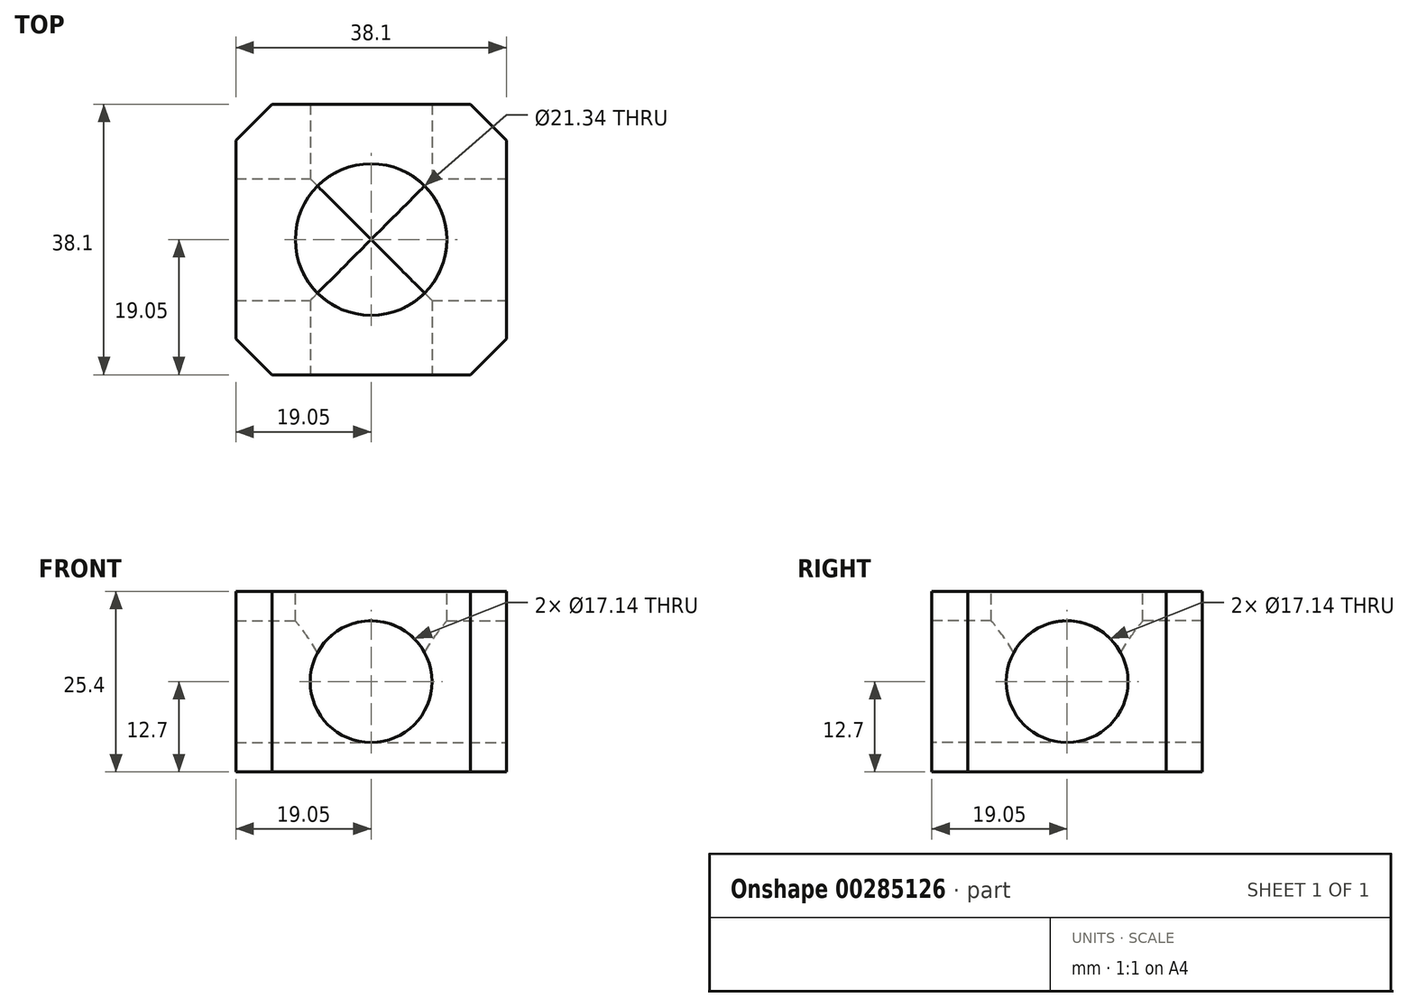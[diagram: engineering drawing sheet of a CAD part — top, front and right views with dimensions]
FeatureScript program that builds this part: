
annotation { "Feature Type Name" : "Feature", "Feature Type Description" : "" }
export const myFeature = defineFeature(function(context is Context, id is Id, definition is map)
    precondition{}
    {
        {
            var Q0;
            Q0=qCreatedBy(makeId("Top.planeOp"),FACE);
            var sketch = newSketch(context, id + "F0", { "sketchPlane" : qUnion([Q0])});
            skLineSegment(sketch, "E0.bottom", {"start": v(19.05, -19.05) * mm, "end": v(-19.05, -19.05) * mm});
            skLineSegment(sketch, "E0.top", {"start": v(19.05, 19.05) * mm, "end": v(-19.05, 19.05) * mm});
            skLineSegment(sketch, "E0.left", {"start": v(19.05, -19.05) * mm, "end": v(19.05, 19.05) * mm});
            skLineSegment(sketch, "E0.right", {"start": v(-19.05, -19.05) * mm, "end": v(-19.05, 19.05) * mm});
            skPoint(sketch, "E0.middle", {"position": v(0, 0) * mm});
            skSolve(sketch);
        }
        {
            var Q0;
            Q0=qSketchRegion(id+"F0",true);
            extrude(context, id + "F1", {"entities" : qUnion([Q0]), "depth" : 25.4 * mm});
        }
        {
            var Q0;
            Q0=makeQuery(id+"F1.opExtrude","CAP_FACE",FACE,{"disambiguationData":[OSD([sQuery(id+"F0.wireOp",EDGE,"E0.bottom"),sQuery(id+"F0.wireOp",EDGE,"E0.top"),sQuery(id+"F0.wireOp",EDGE,"E0.left"),sQuery(id+"F0.wireOp",EDGE,"E0.right")])],"isStart":false});
            var sketch = newSketch(context, id + "F2", { "sketchPlane" : qUnion([Q0])});
            skCircle(sketch, "E1", {"center": v(0, 0) * mm, "radius": 10.67 * mm});
            skSolve(sketch);
        }
        {
            var Q0;
            Q0=makeQuery(id+"F1.opExtrude","SWEPT_FACE",FACE,{"disambiguationData":[OSD([sQuery(id+"F0.wireOp",EDGE,"E0.bottom")])]});
            var sketch = newSketch(context, id + "F3", { "sketchPlane" : qUnion([Q0])});
            skLineSegment(sketch, "E2", {"start": v(0, 0) * mm, "end": v(0, 25.4) * mm});
            skLineSegment(sketch, "E3", {"start": v(0, 25.4) * mm, "end": v(0, 12.7) * mm});
            skCircle(sketch, "E4", {"center": v(0, 12.7) * mm, "radius": 8.57 * mm});
            skSolve(sketch);
        }
        {
            var Q0;
            Q0=qSketchRegion(id+"F3",true);
            extrude(context, id + "F4", {"entities" : qUnion([Q0]), "operationType" : NewBodyOperationType.REMOVE, "oppositeDirection" : true, "depth" : 76.2 * mm});
        }
        {
            var Q0;
            Q0=makeQuery(id+"F1.opExtrude","SWEPT_FACE",FACE,{"disambiguationData":[OSD([sQuery(id+"F0.wireOp",EDGE,"E0.left")])]});
            var sketch = newSketch(context, id + "F5", { "sketchPlane" : qUnion([Q0])});
            skLineSegment(sketch, "E5", {"start": v(0, 0) * mm, "end": v(0, 25.4) * mm});
            skLineSegment(sketch, "E6", {"start": v(0, 25.4) * mm, "end": v(0, 12.7) * mm});
            skCircle(sketch, "E7", {"center": v(0, 12.7) * mm, "radius": 8.57 * mm});
            skSolve(sketch);
        }
        {
            var Q0;
            Q0=qSketchRegion(id+"F5",true);
            extrude(context, id + "F6", {"entities" : qUnion([Q0]), "operationType" : NewBodyOperationType.REMOVE, "oppositeDirection" : true, "depth" : 76.2 * mm});
        }
        {
            var Q0;
            Q0=makeQuery(id+"F2.imprint","IMPRINT",FACE,{"disambiguationData":[TD([[makeQuery(id+"F2.imprint","IMPRINT",EDGE,{"derivedFrom":sQuery(id+"F2.wireOp",EDGE,"E1")}),1.0]])]});
            extrude(context, id + "F7", {"entities" : qUnion([Q0]), "operationType" : NewBodyOperationType.REMOVE, "oppositeDirection" : true, "depth" : 12.7 * mm});
        }
        {
            var Q0;
            Q0=makeQuery(id+"F1.opExtrude","SWEPT_EDGE",EDGE,{"disambiguationData":[OSD([sQuery(id+"F0.wireOp",EDGE,"E0.top"),sQuery(id+"F0.wireOp",EDGE,"E0.right")])]});
            var Q1;
            Q1=makeQuery(id+"F1.opExtrude","SWEPT_EDGE",EDGE,{"disambiguationData":[OSD([sQuery(id+"F0.wireOp",EDGE,"E0.top"),sQuery(id+"F0.wireOp",EDGE,"E0.left")])]});
            var Q2;
            Q2=makeQuery(id+"F1.opExtrude","SWEPT_EDGE",EDGE,{"disambiguationData":[OSD([sQuery(id+"F0.wireOp",EDGE,"E0.bottom"),sQuery(id+"F0.wireOp",EDGE,"E0.left")])]});
            var Q3;
            Q3=makeQuery(id+"F1.opExtrude","SWEPT_EDGE",EDGE,{"disambiguationData":[OSD([sQuery(id+"F0.wireOp",EDGE,"E0.bottom"),sQuery(id+"F0.wireOp",EDGE,"E0.right")])]});
            chamfer(context, id + "F8", {"entities" : qUnion([Q0, Q1, Q2, Q3]), "width" : 5.08 * mm, "tangentPropagation" : true});
        }
    });
